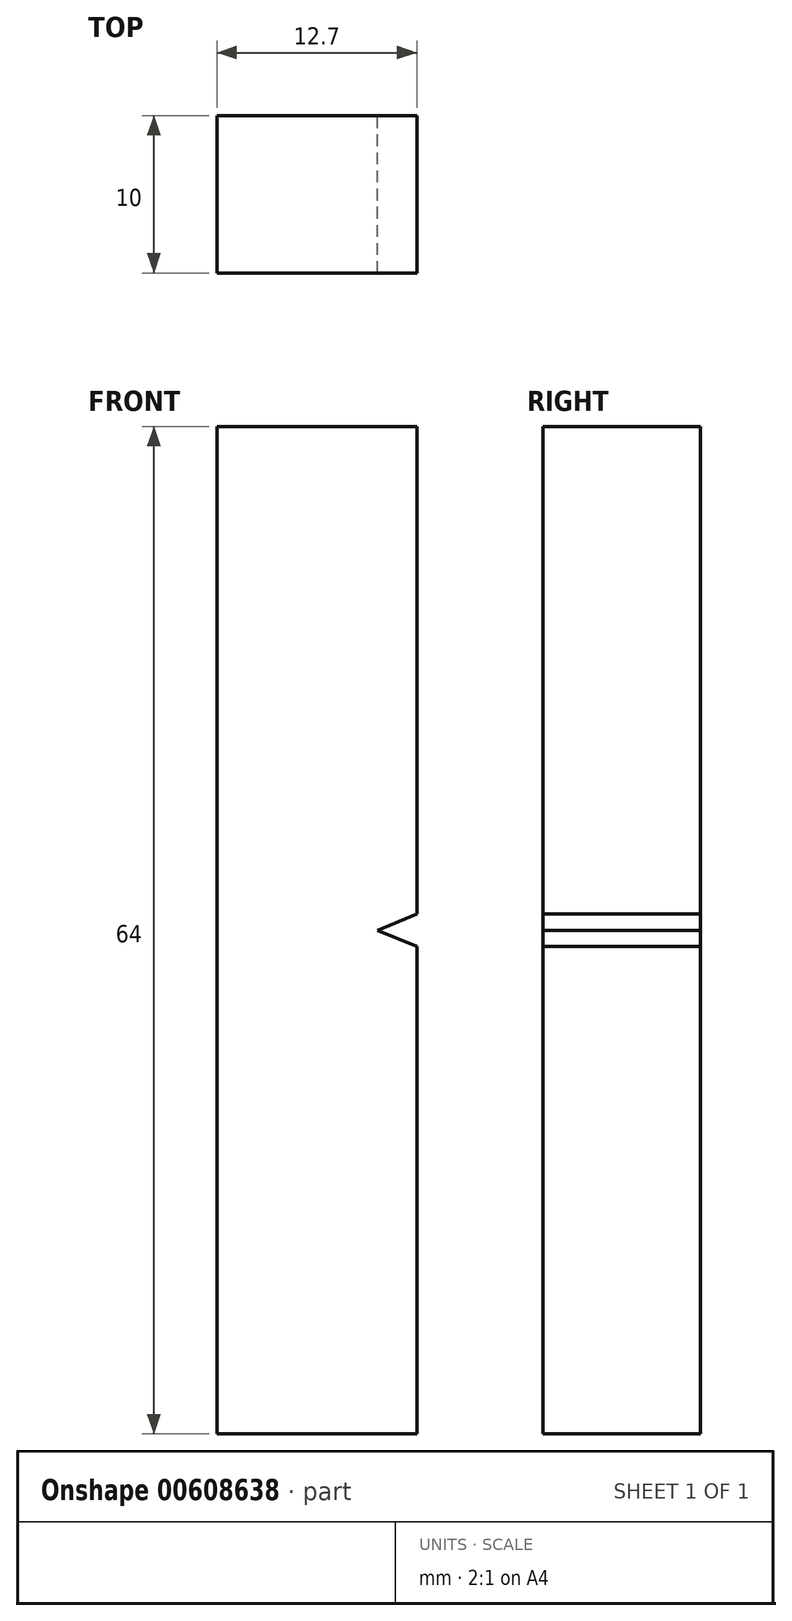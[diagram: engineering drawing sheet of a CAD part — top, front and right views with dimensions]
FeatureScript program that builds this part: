
annotation { "Feature Type Name" : "Feature", "Feature Type Description" : "" }
export const myFeature = defineFeature(function(context is Context, id is Id, definition is map)
    precondition{}
    {
        {
            var Q0;
            Q0=qCreatedBy(makeId("Front.planeOp"),FACE);
            var sketch = newSketch(context, id + "F0", { "sketchPlane" : qUnion([Q0])});
            skLineSegment(sketch, "E0.bottom", {"start": v(-6.35, 32) * mm, "end": v(6.35, 32) * mm});
            skLineSegment(sketch, "E0.top", {"start": v(-6.35, -32) * mm, "end": v(6.35, -32) * mm});
            skLineSegment(sketch, "E0.left", {"start": v(-6.35, 32) * mm, "end": v(-6.35, -32) * mm});
            skLineSegment(sketch, "E0.right", {"start": v(6.35, 32) * mm, "end": v(6.35, 1.04) * mm});
            skLineSegment(sketch, "E1", {"start": v(6.35, 1.04) * mm, "end": v(3.85, 0) * mm});
            skLineSegment(sketch, "E2", {"start": v(3.85, 0) * mm, "end": v(6.35, -1.04) * mm});
            skLineSegment(sketch, "E3.trimOffspring", {"start": v(6.35, -1.04) * mm, "end": v(6.35, -32) * mm});
            skSolve(sketch);
        }
        {
            var Q0;
            Q0=qSketchRegion(id+"F0",true);
            extrude(context, id + "F1", {"entities" : qUnion([Q0]), "endBound" : BoundingType.SYMMETRIC, "depth" : 10 * mm, "offsetDistance" : 25 * mm});
        }
    });
